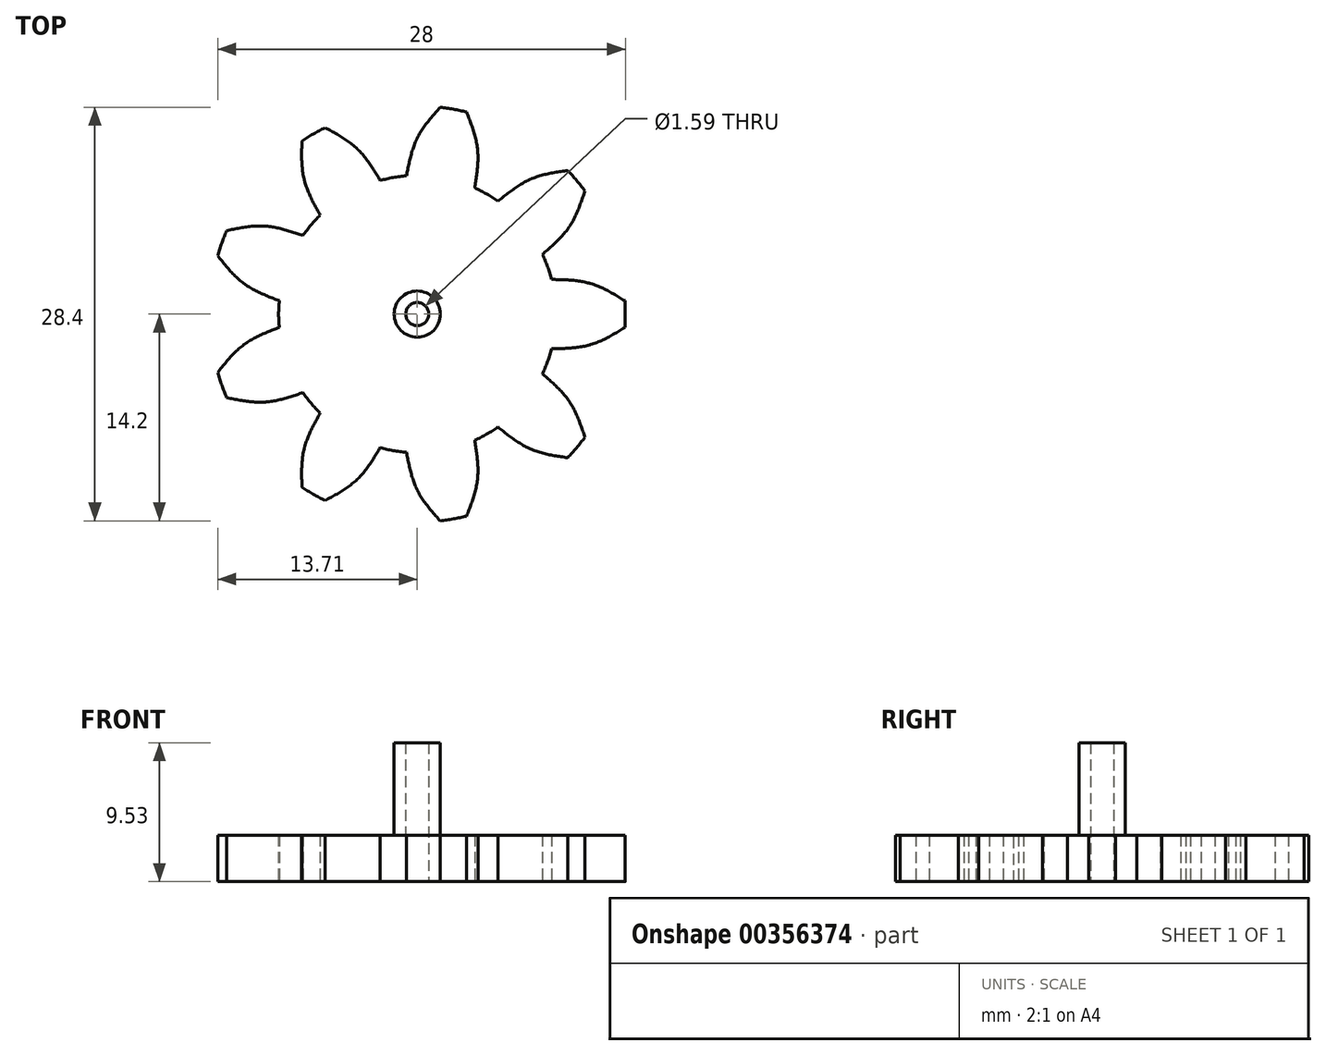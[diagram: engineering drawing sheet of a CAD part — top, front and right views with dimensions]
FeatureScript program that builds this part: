
annotation { "Feature Type Name" : "Feature", "Feature Type Description" : "" }
export const myFeature = defineFeature(function(context is Context, id is Id, definition is map)
    precondition{}
    {
        {
            var Q0;
            Q0=qCreatedBy(makeId("Top.planeOp"),FACE);
            var sketch = newSketch(context, id + "F0", { "sketchPlane" : qUnion([Q0])});
            skCircle(sketch, "E0", {"center": v(0, 0) * mm, "radius": 50.8 * mm});
            skCircle(sketch, "E1", {"center": v(0, 0) * mm, "radius": 63.5 * mm});
            skCircle(sketch, "E2", {"center": v(0, 0) * mm, "radius": 76.2 * mm});
            skLineSegment(sketch, "E3", {"start": v(0, 0) * mm, "end": v(76.2, 0) * mm});
            skCircle(sketch, "E4.cCircle", {"center": v(0, 0) * mm, "radius": 63.5 * mm, "construction": true});
            skLineSegment(sketch, "E4.0", {"start": v(63.5, 11.2) * mm, "end": v(63.5, -11.2) * mm});
            skLineSegment(sketch, "E4.1", {"start": v(63.5, -11.2) * mm, "end": v(55.84, -32.24) * mm});
            skLineSegment(sketch, "E4.2", {"start": v(55.84, -32.24) * mm, "end": v(41.45, -49.4) * mm});
            skLineSegment(sketch, "E4.3", {"start": v(41.45, -49.4) * mm, "end": v(22.05, -60.6) * mm});
            skLineSegment(sketch, "E4.4", {"start": v(22.05, -60.6) * mm, "end": v(0, -64.48) * mm});
            skLineSegment(sketch, "E4.5", {"start": v(0, -64.48) * mm, "end": v(-22.05, -60.6) * mm});
            skLineSegment(sketch, "E4.6", {"start": v(-22.05, -60.6) * mm, "end": v(-41.45, -49.4) * mm});
            skLineSegment(sketch, "E4.7", {"start": v(-41.45, -49.4) * mm, "end": v(-55.84, -32.24) * mm});
            skLineSegment(sketch, "E4.8", {"start": v(-55.84, -32.24) * mm, "end": v(-63.5, -11.2) * mm});
            skLineSegment(sketch, "E4.9", {"start": v(-63.5, -11.2) * mm, "end": v(-63.5, 11.2) * mm});
            skLineSegment(sketch, "E4.10", {"start": v(-63.5, 11.2) * mm, "end": v(-55.84, 32.24) * mm});
            skLineSegment(sketch, "E4.11", {"start": v(-55.84, 32.24) * mm, "end": v(-41.45, 49.4) * mm});
            skLineSegment(sketch, "E4.12", {"start": v(-41.45, 49.4) * mm, "end": v(-22.05, 60.6) * mm});
            skLineSegment(sketch, "E4.13", {"start": v(-22.05, 60.6) * mm, "end": v(0, 64.48) * mm});
            skLineSegment(sketch, "E4.14", {"start": v(0, 64.48) * mm, "end": v(22.05, 60.6) * mm});
            skLineSegment(sketch, "E4.15", {"start": v(22.05, 60.6) * mm, "end": v(41.45, 49.4) * mm});
            skLineSegment(sketch, "E4.16", {"start": v(41.45, 49.4) * mm, "end": v(55.84, 32.24) * mm});
            skLineSegment(sketch, "E4.17", {"start": v(55.84, 32.24) * mm, "end": v(63.5, 11.2) * mm});
            skPoint(sketch, "E4.0.midPoint", {"position": v(63.5, 0) * mm});
            skLineSegment(sketch, "E5.0", {"start": v(49.19, 12.7) * mm, "end": v(49.19, -12.7) * mm});
            skLineSegment(sketch, "E5.1", {"start": v(49.19, -12.7) * mm, "end": v(45.84, -21.89) * mm});
            skLineSegment(sketch, "E5.2", {"start": v(45.84, -21.89) * mm, "end": v(29.52, -41.35) * mm});
            skLineSegment(sketch, "E5.3", {"start": v(29.52, -41.35) * mm, "end": v(21.05, -46.23) * mm});
            skLineSegment(sketch, "E5.4", {"start": v(21.05, -46.23) * mm, "end": v(-3.97, -50.64) * mm});
            skLineSegment(sketch, "E5.5", {"start": v(-3.97, -50.64) * mm, "end": v(-13.6, -48.95) * mm});
            skLineSegment(sketch, "E5.6", {"start": v(-13.6, -48.95) * mm, "end": v(-35.6, -36.25) * mm});
            skLineSegment(sketch, "E5.7", {"start": v(-35.6, -36.25) * mm, "end": v(-41.88, -28.76) * mm});
            skLineSegment(sketch, "E5.8", {"start": v(-41.88, -28.76) * mm, "end": v(-50.56, -4.89) * mm});
            skLineSegment(sketch, "E5.9", {"start": v(-50.56, -4.89) * mm, "end": v(-50.56, 4.89) * mm});
            skLineSegment(sketch, "E5.10", {"start": v(-50.56, 4.89) * mm, "end": v(-41.88, 28.76) * mm});
            skLineSegment(sketch, "E5.11", {"start": v(-41.88, 28.76) * mm, "end": v(-35.6, 36.25) * mm});
            skLineSegment(sketch, "E5.12", {"start": v(-35.6, 36.25) * mm, "end": v(-13.6, 48.95) * mm});
            skLineSegment(sketch, "E5.13", {"start": v(-13.6, 48.95) * mm, "end": v(-3.97, 50.64) * mm});
            skLineSegment(sketch, "E5.14", {"start": v(-3.97, 50.64) * mm, "end": v(21.05, 46.23) * mm});
            skLineSegment(sketch, "E5.15", {"start": v(21.05, 46.23) * mm, "end": v(29.52, 41.35) * mm});
            skLineSegment(sketch, "E5.16", {"start": v(29.52, 41.35) * mm, "end": v(45.84, 21.89) * mm});
            skLineSegment(sketch, "E5.17", {"start": v(45.84, 21.89) * mm, "end": v(49.19, 12.7) * mm});
            skPoint(sketch, "E5.0.midPoint", {"position": v(49.19, 0) * mm});
            skLineSegment(sketch, "E6", {"start": v(0, 0) * mm, "end": v(58.37, 48.98) * mm});
            skLineSegment(sketch, "E7", {"start": v(0, 0) * mm, "end": v(13.23, 75.04) * mm});
            skLineSegment(sketch, "E8", {"start": v(0, 0) * mm, "end": v(-38.1, 66) * mm});
            skLineSegment(sketch, "E9", {"start": v(0, 0) * mm, "end": v(-71.6, 26.06) * mm});
            skLineSegment(sketch, "E10", {"start": v(0, 0) * mm, "end": v(-71.6, -26.06) * mm});
            skLineSegment(sketch, "E11", {"start": v(0, 0) * mm, "end": v(-38.1, -66) * mm});
            skLineSegment(sketch, "E12", {"start": v(-38.1, -66) * mm, "end": v(0, 0) * mm});
            skLineSegment(sketch, "E13", {"start": v(0, 0) * mm, "end": v(13.23, -75.04) * mm});
            skLineSegment(sketch, "E14", {"start": v(13.23, -75.04) * mm, "end": v(0, 0) * mm});
            skLineSegment(sketch, "E15", {"start": v(0, 0) * mm, "end": v(58.37, -48.98) * mm});
            skLineSegment(sketch, "E16", {"start": v(76.04, 4.89) * mm, "end": v(76.04, -4.89) * mm});
            skLineSegment(sketch, "E17", {"start": v(61.4, -45.13) * mm, "end": v(55.1, -52.62) * mm});
            skLineSegment(sketch, "E18", {"start": v(8.4, -75.74) * mm, "end": v(18.02, -74.04) * mm});
            skLineSegment(sketch, "E19", {"start": v(-42.26, -63.41) * mm, "end": v(-33.79, -68.3) * mm});
            skLineSegment(sketch, "E20", {"start": v(-73.13, -21.41) * mm, "end": v(-69.78, -30.6) * mm});
            skLineSegment(sketch, "E21", {"start": v(-73.13, 21.41) * mm, "end": v(-69.78, 30.6) * mm});
            skLineSegment(sketch, "E22", {"start": v(-42.26, 63.41) * mm, "end": v(-33.79, 68.3) * mm});
            skLineSegment(sketch, "E23", {"start": v(8.4, 75.74) * mm, "end": v(18.02, 74.04) * mm});
            skLineSegment(sketch, "E24", {"start": v(55.1, 52.62) * mm, "end": v(61.4, 45.13) * mm});
            skFitSpline(sketch, "E25", {"points": [v(-42.26, 63.41) * mm, v(-41.45, 49.4) * mm, v(-35.6, 36.25) * mm], "startDerivative": vector(-0.86, -28.72) * mm, "endDerivative": vector(14.16, -25.61) * mm});
            skFitSpline(sketch, "E26", {"points": [v(-33.79, 68.3) * mm, v(-22.05, 60.6) * mm, v(-13.6, 48.95) * mm], "startDerivative": vector(25.3, -13.62) * mm, "endDerivative": vector(15.1, -25.06) * mm});
            skFitSpline(sketch, "E27", {"points": [v(8.4, 75.74) * mm, v(0, 64.48) * mm, v(-3.97, 50.64) * mm], "startDerivative": vector(-19.12, -21.45) * mm, "endDerivative": vector(-5.62, -28.72) * mm});
            skFitSpline(sketch, "E28", {"points": [v(18.02, 74.04) * mm, v(22.05, 60.6) * mm, v(21.05, 46.23) * mm], "startDerivative": vector(10.63, -26.7) * mm, "endDerivative": vector(-4.54, -28.9) * mm});
            skFitSpline(sketch, "E29", {"points": [v(29.52, 41.35) * mm, v(41.45, 49.4) * mm, v(55.1, 52.62) * mm], "startDerivative": vector(22.76, 18.39) * mm, "endDerivative": vector(28.44, 4.14) * mm});
            skFitSpline(sketch, "E30", {"points": [v(61.4, 45.13) * mm, v(55.84, 32.24) * mm, v(45.84, 21.89) * mm], "startDerivative": vector(-9.02, -27.29) * mm, "endDerivative": vector(-22.06, -19.22) * mm});
            skFitSpline(sketch, "E31", {"points": [v(49.19, 12.7) * mm, v(63.5, 11.2) * mm, v(76.04, 4.89) * mm], "startDerivative": vector(29.26, -0.55) * mm, "endDerivative": vector(24.45, -15.1) * mm});
            skFitSpline(sketch, "E32", {"points": [v(76.04, -4.89) * mm, v(63.5, -11.2) * mm, v(49.19, -12.7) * mm], "startDerivative": vector(-24.45, -15.1) * mm, "endDerivative": vector(-29.26, -0.55) * mm});
            skFitSpline(sketch, "E33", {"points": [v(45.84, -21.89) * mm, v(55.84, -32.24) * mm, v(61.4, -45.13) * mm], "startDerivative": vector(22.06, -19.22) * mm, "endDerivative": vector(9.02, -27.29) * mm});
            skFitSpline(sketch, "E34", {"points": [v(29.52, -41.35) * mm, v(41.45, -49.4) * mm, v(55.1, -52.62) * mm], "startDerivative": vector(22.76, -18.39) * mm, "endDerivative": vector(28.44, -4.14) * mm});
            skFitSpline(sketch, "E35", {"points": [v(21.05, -46.23) * mm, v(22.05, -60.6) * mm, v(18.02, -74.04) * mm], "startDerivative": vector(4.54, -28.9) * mm, "endDerivative": vector(-10.63, -26.7) * mm});
            skFitSpline(sketch, "E36", {"points": [v(-3.97, -50.64) * mm, v(0, -64.48) * mm, v(8.4, -75.74) * mm], "startDerivative": vector(5.62, -28.72) * mm, "endDerivative": vector(19.12, -21.45) * mm});
            skFitSpline(sketch, "E37", {"points": [v(-13.6, -48.95) * mm, v(-22.05, -60.6) * mm, v(-33.79, -68.3) * mm], "startDerivative": vector(-15.1, -25.06) * mm, "endDerivative": vector(-25.3, -13.62) * mm});
            skFitSpline(sketch, "E38", {"points": [v(-35.6, -36.25) * mm, v(-41.45, -49.4) * mm, v(-42.26, -63.41) * mm], "startDerivative": vector(-14.16, -25.61) * mm, "endDerivative": vector(0.86, -28.72) * mm});
            skFitSpline(sketch, "E39", {"points": [v(-41.88, -28.76) * mm, v(-55.84, -32.24) * mm, v(-69.78, -30.6) * mm], "startDerivative": vector(-27.68, -9.5) * mm, "endDerivative": vector(-28.14, 5.83) * mm});
            skFitSpline(sketch, "E40", {"points": [v(-50.56, -4.89) * mm, v(-63.5, -11.2) * mm, v(-73.13, -21.41) * mm], "startDerivative": vector(-27.3, -10.52) * mm, "endDerivative": vector(-17.8, -22.56) * mm});
            skFitSpline(sketch, "E41", {"points": [v(-41.88, 28.76) * mm, v(-55.84, 32.24) * mm, v(-69.78, 30.6) * mm], "startDerivative": vector(-27.68, 9.5) * mm, "endDerivative": vector(-28.14, -5.83) * mm});
            skFitSpline(sketch, "E42", {"points": [v(-73.13, 21.41) * mm, v(-63.5, 11.2) * mm, v(-50.56, 4.89) * mm], "startDerivative": vector(17.8, -22.56) * mm, "endDerivative": vector(27.3, -10.52) * mm});
            skSolve(sketch);
        }
        {
            var Q0;
            {var subQ0=sQuery(id+"F0.wireOp",EDGE,"E5.2");var subQ3=sQuery(id+"F0.wireOp",EDGE,"E15");var subQ5=makeQuery(id+"F0.imprint","INTERSECT",VERTEX,{"derivedFrom":[subQ0,subQ3]});Q0=makeQuery(id+"F0.imprint","IMPRINT",FACE,{"disambiguationData":[TD([[makeQuery(id+"F0.imprint","IMPRINT",EDGE,{"disambiguationData":[TD([[subQ5,-1.0]])],"derivedFrom":subQ3}),1.0]])]});}
            var Q1;
            {var subQ1=sQuery(id+"F0.wireOp",EDGE,"E5.11");Q1=makeQuery(id+"F0.imprint","IMPRINT",FACE,{"disambiguationData":[TD([[makeQuery(id+"F0.imprint","IMPRINT",EDGE,{"derivedFrom":subQ1}),-1.0]])]});}
            var Q2;
            {var subQ0=sQuery(id+"F0.wireOp",EDGE,"E40");var subQ5=sQuery(id+"F0.wireOp",EDGE,"E1");var subQ7=makeQuery(id+"F0.imprint","INTERSECT",VERTEX,{"derivedFrom":[subQ5,subQ0]});Q2=makeQuery(id+"F0.imprint","IMPRINT",FACE,{"disambiguationData":[TD([[makeQuery(id+"F0.imprint","IMPRINT",EDGE,{"disambiguationData":[TD([[subQ7,-1.0]])],"derivedFrom":subQ5}),1.0]])]});}
            var Q3;
            {var subQ0=sQuery(id+"F0.wireOp",EDGE,"E11");var subQ5=sQuery(id+"F0.wireOp",EDGE,"E19");var subQ7=makeQuery(id+"F0.imprint","INTERSECT",VERTEX,{"derivedFrom":[subQ0,subQ5]});Q3=makeQuery(id+"F0.imprint","IMPRINT",FACE,{"disambiguationData":[TD([[makeQuery(id+"F0.imprint","IMPRINT",EDGE,{"disambiguationData":[TD([[subQ7,1.0]])],"derivedFrom":subQ0}),-1.0]])]});}
            var Q4;
            {var subQ0=sQuery(id+"F0.wireOp",EDGE,"E8");var subQ5=sQuery(id+"F0.wireOp",EDGE,"E22");var subQ7=makeQuery(id+"F0.imprint","INTERSECT",VERTEX,{"derivedFrom":[subQ0,subQ5]});Q4=makeQuery(id+"F0.imprint","IMPRINT",FACE,{"disambiguationData":[TD([[makeQuery(id+"F0.imprint","IMPRINT",EDGE,{"disambiguationData":[TD([[subQ7,1.0]])],"derivedFrom":subQ0}),-1.0]])]});}
            var Q5;
            {var subQ3=sQuery(id+"F0.wireOp",EDGE,"E7");var subQ5=sQuery(id+"F0.wireOp",EDGE,"E23");var subQ6=makeQuery(id+"F0.imprint","INTERSECT",VERTEX,{"derivedFrom":[subQ3,subQ5]});Q5=makeQuery(id+"F0.imprint","IMPRINT",FACE,{"disambiguationData":[TD([[makeQuery(id+"F0.imprint","IMPRINT",EDGE,{"disambiguationData":[TD([[subQ6,1.0]])],"derivedFrom":subQ3}),-1.0]])]});}
            var Q6;
            {var subQ3=sQuery(id+"F0.wireOp",EDGE,"E13");var subQ5=sQuery(id+"F0.wireOp",EDGE,"E18");var subQ6=makeQuery(id+"F0.imprint","INTERSECT",VERTEX,{"derivedFrom":[subQ3,subQ5]});Q6=makeQuery(id+"F0.imprint","IMPRINT",FACE,{"disambiguationData":[TD([[makeQuery(id+"F0.imprint","IMPRINT",EDGE,{"disambiguationData":[TD([[subQ6,1.0]])],"derivedFrom":subQ3}),-1.0]])]});}
            var Q7;
            {var subQ5=sQuery(id+"F0.wireOp",EDGE,"E5.9");Q7=makeQuery(id+"F0.imprint","IMPRINT",FACE,{"disambiguationData":[TD([[makeQuery(id+"F0.imprint","IMPRINT",EDGE,{"derivedFrom":subQ5}),-1.0]])]});}
            var Q8;
            {var subQ0=sQuery(id+"F0.wireOp",EDGE,"E32");var subQ5=sQuery(id+"F0.wireOp",EDGE,"E1");var subQ7=makeQuery(id+"F0.imprint","INTERSECT",VERTEX,{"derivedFrom":[subQ5,subQ0]});Q8=makeQuery(id+"F0.imprint","IMPRINT",FACE,{"disambiguationData":[TD([[makeQuery(id+"F0.imprint","IMPRINT",EDGE,{"disambiguationData":[TD([[subQ7,-1.0]])],"derivedFrom":subQ5}),1.0]])]});}
            var Q9;
            {var subQ3=sQuery(id+"F0.wireOp",EDGE,"E10");var subQ5=sQuery(id+"F0.wireOp",EDGE,"E20");var subQ7=makeQuery(id+"F0.imprint","INTERSECT",VERTEX,{"derivedFrom":[subQ3,subQ5]});Q9=makeQuery(id+"F0.imprint","IMPRINT",FACE,{"disambiguationData":[TD([[makeQuery(id+"F0.imprint","IMPRINT",EDGE,{"disambiguationData":[TD([[subQ7,1.0]])],"derivedFrom":subQ3}),1.0]])]});}
            var Q10;
            {var subQ1=sQuery(id+"F0.wireOp",EDGE,"E0");var subQ3=sQuery(id+"F0.wireOp",EDGE,"E9");var subQ4=makeQuery(id+"F0.imprint","INTERSECT",VERTEX,{"derivedFrom":[subQ1,subQ3]});Q10=makeQuery(id+"F0.imprint","IMPRINT",FACE,{"disambiguationData":[TD([[makeQuery(id+"F0.imprint","IMPRINT",EDGE,{"disambiguationData":[TD([[subQ4,1.0]])],"derivedFrom":subQ3}),-1.0]])]});}
            var Q11;
            {var subQ0=sQuery(id+"F0.wireOp",EDGE,"E5.17");Q11=makeQuery(id+"F0.imprint","IMPRINT",FACE,{"disambiguationData":[TD([[makeQuery(id+"F0.imprint","IMPRINT",EDGE,{"derivedFrom":subQ0}),-1.0]])]});}
            var Q12;
            {var subQ5=sQuery(id+"F0.wireOp",EDGE,"E5.7");Q12=makeQuery(id+"F0.imprint","IMPRINT",FACE,{"disambiguationData":[TD([[makeQuery(id+"F0.imprint","IMPRINT",EDGE,{"derivedFrom":subQ5}),-1.0]])]});}
            var Q13;
            {var subQ0=sQuery(id+"F0.wireOp",EDGE,"E33");var subQ5=sQuery(id+"F0.wireOp",EDGE,"E1");var subQ7=makeQuery(id+"F0.imprint","INTERSECT",VERTEX,{"derivedFrom":[subQ5,subQ0]});Q13=makeQuery(id+"F0.imprint","IMPRINT",FACE,{"disambiguationData":[TD([[makeQuery(id+"F0.imprint","IMPRINT",EDGE,{"disambiguationData":[TD([[subQ7,1.0]])],"derivedFrom":subQ5}),1.0]])]});}
            var Q14;
            {var subQ0=sQuery(id+"F0.wireOp",EDGE,"E27");var subQ5=sQuery(id+"F0.wireOp",EDGE,"E1");var subQ6=makeQuery(id+"F0.imprint","INTERSECT",VERTEX,{"derivedFrom":[subQ5,subQ0]});Q14=makeQuery(id+"F0.imprint","IMPRINT",FACE,{"disambiguationData":[TD([[makeQuery(id+"F0.imprint","IMPRINT",EDGE,{"disambiguationData":[TD([[subQ6,1.0]])],"derivedFrom":subQ5}),1.0]])]});}
            var Q15;
            {var subQ3=sQuery(id+"F0.wireOp",EDGE,"E6");var subQ5=sQuery(id+"F0.wireOp",EDGE,"E24");var subQ6=makeQuery(id+"F0.imprint","INTERSECT",VERTEX,{"derivedFrom":[subQ3,subQ5]});Q15=makeQuery(id+"F0.imprint","IMPRINT",FACE,{"disambiguationData":[TD([[makeQuery(id+"F0.imprint","IMPRINT",EDGE,{"disambiguationData":[TD([[subQ6,1.0]])],"derivedFrom":subQ3}),1.0]])]});}
            var Q16;
            {var subQ1=sQuery(id+"F0.wireOp",EDGE,"E0");var subQ3=sQuery(id+"F0.wireOp",EDGE,"E13");var subQ4=makeQuery(id+"F0.imprint","INTERSECT",VERTEX,{"derivedFrom":[subQ1,subQ3]});Q16=makeQuery(id+"F0.imprint","IMPRINT",FACE,{"disambiguationData":[TD([[makeQuery(id+"F0.imprint","IMPRINT",EDGE,{"disambiguationData":[TD([[subQ4,1.0]])],"derivedFrom":subQ3}),-1.0]])]});}
            var Q17;
            {var subQ0=sQuery(id+"F0.wireOp",EDGE,"E16");var subQ1=sQuery(id+"F0.wireOp",EDGE,"E3");var subQ2=makeQuery(id+"F0.imprint","INTERSECT",VERTEX,{"derivedFrom":[subQ1,subQ0]});Q17=makeQuery(id+"F0.imprint","IMPRINT",FACE,{"disambiguationData":[TD([[makeQuery(id+"F0.imprint","IMPRINT",EDGE,{"disambiguationData":[TD([[subQ2,1.0]])],"derivedFrom":subQ1}),1.0]])]});}
            var Q18;
            {var subQ0=sQuery(id+"F0.wireOp",EDGE,"E15");var subQ5=sQuery(id+"F0.wireOp",EDGE,"E17");var subQ6=makeQuery(id+"F0.imprint","INTERSECT",VERTEX,{"derivedFrom":[subQ0,subQ5]});Q18=makeQuery(id+"F0.imprint","IMPRINT",FACE,{"disambiguationData":[TD([[makeQuery(id+"F0.imprint","IMPRINT",EDGE,{"disambiguationData":[TD([[subQ6,1.0]])],"derivedFrom":subQ0}),1.0]])]});}
            var Q19;
            {var subQ1=sQuery(id+"F0.wireOp",EDGE,"E0");var subQ3=sQuery(id+"F0.wireOp",EDGE,"E13");var subQ4=makeQuery(id+"F0.imprint","INTERSECT",VERTEX,{"derivedFrom":[subQ1,subQ3]});Q19=makeQuery(id+"F0.imprint","IMPRINT",FACE,{"disambiguationData":[TD([[makeQuery(id+"F0.imprint","IMPRINT",EDGE,{"disambiguationData":[TD([[subQ4,1.0]])],"derivedFrom":subQ3}),1.0]])]});}
            var Q20;
            {var subQ1=sQuery(id+"F0.wireOp",EDGE,"E0");var subQ3=sQuery(id+"F0.wireOp",EDGE,"E10");var subQ4=makeQuery(id+"F0.imprint","INTERSECT",VERTEX,{"derivedFrom":[subQ1,subQ3]});Q20=makeQuery(id+"F0.imprint","IMPRINT",FACE,{"disambiguationData":[TD([[makeQuery(id+"F0.imprint","IMPRINT",EDGE,{"disambiguationData":[TD([[subQ4,1.0]])],"derivedFrom":subQ3}),-1.0]])]});}
            var Q21;
            {var subQ1=sQuery(id+"F0.wireOp",EDGE,"E0");var subQ3=sQuery(id+"F0.wireOp",EDGE,"E7");var subQ4=makeQuery(id+"F0.imprint","INTERSECT",VERTEX,{"derivedFrom":[subQ1,subQ3]});Q21=makeQuery(id+"F0.imprint","IMPRINT",FACE,{"disambiguationData":[TD([[makeQuery(id+"F0.imprint","IMPRINT",EDGE,{"disambiguationData":[TD([[subQ4,1.0]])],"derivedFrom":subQ3}),-1.0]])]});}
            var Q22;
            {var subQ0=sQuery(id+"F0.wireOp",EDGE,"E5.1");Q22=makeQuery(id+"F0.imprint","IMPRINT",FACE,{"disambiguationData":[TD([[makeQuery(id+"F0.imprint","IMPRINT",EDGE,{"derivedFrom":subQ0}),-1.0]])]});}
            var Q23;
            {var subQ3=sQuery(id+"F0.wireOp",EDGE,"E9");var subQ5=sQuery(id+"F0.wireOp",EDGE,"E21");var subQ6=makeQuery(id+"F0.imprint","INTERSECT",VERTEX,{"derivedFrom":[subQ3,subQ5]});Q23=makeQuery(id+"F0.imprint","IMPRINT",FACE,{"disambiguationData":[TD([[makeQuery(id+"F0.imprint","IMPRINT",EDGE,{"disambiguationData":[TD([[subQ6,1.0]])],"derivedFrom":subQ3}),1.0]])]});}
            var Q24;
            {var subQ0=sQuery(id+"F0.wireOp",EDGE,"E31");var subQ5=sQuery(id+"F0.wireOp",EDGE,"E1");var subQ6=makeQuery(id+"F0.imprint","INTERSECT",VERTEX,{"derivedFrom":[subQ5,subQ0]});Q24=makeQuery(id+"F0.imprint","IMPRINT",FACE,{"disambiguationData":[TD([[makeQuery(id+"F0.imprint","IMPRINT",EDGE,{"disambiguationData":[TD([[subQ6,1.0]])],"derivedFrom":subQ5}),1.0]])]});}
            var Q25;
            {var subQ0=sQuery(id+"F0.wireOp",EDGE,"E37");var subQ5=sQuery(id+"F0.wireOp",EDGE,"E1");var subQ7=makeQuery(id+"F0.imprint","INTERSECT",VERTEX,{"derivedFrom":[subQ5,subQ0]});Q25=makeQuery(id+"F0.imprint","IMPRINT",FACE,{"disambiguationData":[TD([[makeQuery(id+"F0.imprint","IMPRINT",EDGE,{"disambiguationData":[TD([[subQ7,1.0]])],"derivedFrom":subQ5}),1.0]])]});}
            var Q26;
            {var subQ1=sQuery(id+"F0.wireOp",EDGE,"E0");var subQ3=sQuery(id+"F0.wireOp",EDGE,"E6");var subQ4=makeQuery(id+"F0.imprint","INTERSECT",VERTEX,{"derivedFrom":[subQ1,subQ3]});Q26=makeQuery(id+"F0.imprint","IMPRINT",FACE,{"disambiguationData":[TD([[makeQuery(id+"F0.imprint","IMPRINT",EDGE,{"disambiguationData":[TD([[subQ4,1.0]])],"derivedFrom":subQ3}),-1.0]])]});}
            var Q27;
            {var subQ5=sQuery(id+"F0.wireOp",EDGE,"E5.13");Q27=makeQuery(id+"F0.imprint","IMPRINT",FACE,{"disambiguationData":[TD([[makeQuery(id+"F0.imprint","IMPRINT",EDGE,{"derivedFrom":subQ5}),-1.0]])]});}
            var Q28;
            {var subQ0=sQuery(id+"F0.wireOp",EDGE,"E39");var subQ5=sQuery(id+"F0.wireOp",EDGE,"E1");var subQ7=makeQuery(id+"F0.imprint","INTERSECT",VERTEX,{"derivedFrom":[subQ5,subQ0]});Q28=makeQuery(id+"F0.imprint","IMPRINT",FACE,{"disambiguationData":[TD([[makeQuery(id+"F0.imprint","IMPRINT",EDGE,{"disambiguationData":[TD([[subQ7,1.0]])],"derivedFrom":subQ5}),1.0]])]});}
            var Q29;
            {var subQ0=sQuery(id+"F0.wireOp",EDGE,"E29");var subQ5=sQuery(id+"F0.wireOp",EDGE,"E1");var subQ6=makeQuery(id+"F0.imprint","INTERSECT",VERTEX,{"derivedFrom":[subQ5,subQ0]});Q29=makeQuery(id+"F0.imprint","IMPRINT",FACE,{"disambiguationData":[TD([[makeQuery(id+"F0.imprint","IMPRINT",EDGE,{"disambiguationData":[TD([[subQ6,1.0]])],"derivedFrom":subQ5}),1.0]])]});}
            var Q30;
            {var subQ1=sQuery(id+"F0.wireOp",EDGE,"E0");var subQ3=sQuery(id+"F0.wireOp",EDGE,"E8");var subQ4=makeQuery(id+"F0.imprint","INTERSECT",VERTEX,{"derivedFrom":[subQ1,subQ3]});Q30=makeQuery(id+"F0.imprint","IMPRINT",FACE,{"disambiguationData":[TD([[makeQuery(id+"F0.imprint","IMPRINT",EDGE,{"disambiguationData":[TD([[subQ4,1.0]])],"derivedFrom":subQ3}),-1.0]])]});}
            var Q31;
            {var subQ1=sQuery(id+"F0.wireOp",EDGE,"E0");var subQ3=sQuery(id+"F0.wireOp",EDGE,"E10");var subQ4=makeQuery(id+"F0.imprint","INTERSECT",VERTEX,{"derivedFrom":[subQ1,subQ3]});Q31=makeQuery(id+"F0.imprint","IMPRINT",FACE,{"disambiguationData":[TD([[makeQuery(id+"F0.imprint","IMPRINT",EDGE,{"disambiguationData":[TD([[subQ4,1.0]])],"derivedFrom":subQ3}),1.0]])]});}
            var Q32;
            {var subQ0=sQuery(id+"F0.wireOp",EDGE,"E42");var subQ5=sQuery(id+"F0.wireOp",EDGE,"E1");var subQ6=makeQuery(id+"F0.imprint","INTERSECT",VERTEX,{"derivedFrom":[subQ5,subQ0]});Q32=makeQuery(id+"F0.imprint","IMPRINT",FACE,{"disambiguationData":[TD([[makeQuery(id+"F0.imprint","IMPRINT",EDGE,{"disambiguationData":[TD([[subQ6,1.0]])],"derivedFrom":subQ5}),1.0]])]});}
            var Q33;
            {var subQ0=sQuery(id+"F0.wireOp",EDGE,"E16");var subQ1=sQuery(id+"F0.wireOp",EDGE,"E3");var subQ2=makeQuery(id+"F0.imprint","INTERSECT",VERTEX,{"derivedFrom":[subQ1,subQ0]});Q33=makeQuery(id+"F0.imprint","IMPRINT",FACE,{"disambiguationData":[TD([[makeQuery(id+"F0.imprint","IMPRINT",EDGE,{"disambiguationData":[TD([[subQ2,1.0]])],"derivedFrom":subQ1}),-1.0]])]});}
            var Q34;
            {var subQ1=sQuery(id+"F0.wireOp",EDGE,"E0");var subQ3=sQuery(id+"F0.wireOp",EDGE,"E11");var subQ4=makeQuery(id+"F0.imprint","INTERSECT",VERTEX,{"derivedFrom":[subQ1,subQ3]});Q34=makeQuery(id+"F0.imprint","IMPRINT",FACE,{"disambiguationData":[TD([[makeQuery(id+"F0.imprint","IMPRINT",EDGE,{"disambiguationData":[TD([[subQ4,1.0]])],"derivedFrom":subQ3}),-1.0]])]});}
            var Q35;
            {var subQ0=sQuery(id+"F0.wireOp",EDGE,"E38");var subQ5=sQuery(id+"F0.wireOp",EDGE,"E1");var subQ7=makeQuery(id+"F0.imprint","INTERSECT",VERTEX,{"derivedFrom":[subQ5,subQ0]});Q35=makeQuery(id+"F0.imprint","IMPRINT",FACE,{"disambiguationData":[TD([[makeQuery(id+"F0.imprint","IMPRINT",EDGE,{"disambiguationData":[TD([[subQ7,-1.0]])],"derivedFrom":subQ5}),1.0]])]});}
            var Q36;
            {var subQ1=sQuery(id+"F0.wireOp",EDGE,"E0");var subQ3=sQuery(id+"F0.wireOp",EDGE,"E8");var subQ4=makeQuery(id+"F0.imprint","INTERSECT",VERTEX,{"derivedFrom":[subQ1,subQ3]});Q36=makeQuery(id+"F0.imprint","IMPRINT",FACE,{"disambiguationData":[TD([[makeQuery(id+"F0.imprint","IMPRINT",EDGE,{"disambiguationData":[TD([[subQ4,1.0]])],"derivedFrom":subQ3}),1.0]])]});}
            var Q37;
            {var subQ0=sQuery(id+"F0.wireOp",EDGE,"E26");var subQ5=sQuery(id+"F0.wireOp",EDGE,"E1");var subQ7=makeQuery(id+"F0.imprint","INTERSECT",VERTEX,{"derivedFrom":[subQ5,subQ0]});Q37=makeQuery(id+"F0.imprint","IMPRINT",FACE,{"disambiguationData":[TD([[makeQuery(id+"F0.imprint","IMPRINT",EDGE,{"disambiguationData":[TD([[subQ7,-1.0]])],"derivedFrom":subQ5}),1.0]])]});}
            var Q38;
            {var subQ1=sQuery(id+"F0.wireOp",EDGE,"E0");var subQ3=sQuery(id+"F0.wireOp",EDGE,"E7");var subQ4=makeQuery(id+"F0.imprint","INTERSECT",VERTEX,{"derivedFrom":[subQ1,subQ3]});Q38=makeQuery(id+"F0.imprint","IMPRINT",FACE,{"disambiguationData":[TD([[makeQuery(id+"F0.imprint","IMPRINT",EDGE,{"disambiguationData":[TD([[subQ4,1.0]])],"derivedFrom":subQ3}),1.0]])]});}
            var Q39;
            {var subQ0=sQuery(id+"F0.wireOp",EDGE,"E30");var subQ5=sQuery(id+"F0.wireOp",EDGE,"E1");var subQ7=makeQuery(id+"F0.imprint","INTERSECT",VERTEX,{"derivedFrom":[subQ5,subQ0]});Q39=makeQuery(id+"F0.imprint","IMPRINT",FACE,{"disambiguationData":[TD([[makeQuery(id+"F0.imprint","IMPRINT",EDGE,{"disambiguationData":[TD([[subQ7,-1.0]])],"derivedFrom":subQ5}),1.0]])]});}
            var Q40;
            {var subQ5=sQuery(id+"F0.wireOp",EDGE,"E5.3");Q40=makeQuery(id+"F0.imprint","IMPRINT",FACE,{"disambiguationData":[TD([[makeQuery(id+"F0.imprint","IMPRINT",EDGE,{"derivedFrom":subQ5}),-1.0]])]});}
            var Q41;
            {var subQ1=sQuery(id+"F0.wireOp",EDGE,"E0");var subQ3=sQuery(id+"F0.wireOp",EDGE,"E9");var subQ4=makeQuery(id+"F0.imprint","INTERSECT",VERTEX,{"derivedFrom":[subQ1,subQ3]});Q41=makeQuery(id+"F0.imprint","IMPRINT",FACE,{"disambiguationData":[TD([[makeQuery(id+"F0.imprint","IMPRINT",EDGE,{"disambiguationData":[TD([[subQ4,1.0]])],"derivedFrom":subQ3}),1.0]])]});}
            var Q42;
            {var subQ0=sQuery(id+"F0.wireOp",EDGE,"E28");var subQ5=sQuery(id+"F0.wireOp",EDGE,"E1");var subQ6=makeQuery(id+"F0.imprint","INTERSECT",VERTEX,{"derivedFrom":[subQ5,subQ0]});Q42=makeQuery(id+"F0.imprint","IMPRINT",FACE,{"disambiguationData":[TD([[makeQuery(id+"F0.imprint","IMPRINT",EDGE,{"disambiguationData":[TD([[subQ6,-1.0]])],"derivedFrom":subQ5}),1.0]])]});}
            var Q43;
            {var subQ3=sQuery(id+"F0.wireOp",EDGE,"E7");var subQ5=sQuery(id+"F0.wireOp",EDGE,"E23");var subQ6=makeQuery(id+"F0.imprint","INTERSECT",VERTEX,{"derivedFrom":[subQ3,subQ5]});Q43=makeQuery(id+"F0.imprint","IMPRINT",FACE,{"disambiguationData":[TD([[makeQuery(id+"F0.imprint","IMPRINT",EDGE,{"disambiguationData":[TD([[subQ6,1.0]])],"derivedFrom":subQ3}),1.0]])]});}
            var Q44;
            {var subQ0=sQuery(id+"F0.wireOp",EDGE,"E34");var subQ5=sQuery(id+"F0.wireOp",EDGE,"E1");var subQ7=makeQuery(id+"F0.imprint","INTERSECT",VERTEX,{"derivedFrom":[subQ5,subQ0]});Q44=makeQuery(id+"F0.imprint","IMPRINT",FACE,{"disambiguationData":[TD([[makeQuery(id+"F0.imprint","IMPRINT",EDGE,{"disambiguationData":[TD([[subQ7,-1.0]])],"derivedFrom":subQ5}),1.0]])]});}
            var Q45;
            {var subQ3=sQuery(id+"F0.wireOp",EDGE,"E9");var subQ5=sQuery(id+"F0.wireOp",EDGE,"E21");var subQ7=makeQuery(id+"F0.imprint","INTERSECT",VERTEX,{"derivedFrom":[subQ3,subQ5]});Q45=makeQuery(id+"F0.imprint","IMPRINT",FACE,{"disambiguationData":[TD([[makeQuery(id+"F0.imprint","IMPRINT",EDGE,{"disambiguationData":[TD([[subQ7,1.0]])],"derivedFrom":subQ3}),-1.0]])]});}
            var Q46;
            {var subQ0=sQuery(id+"F0.wireOp",EDGE,"E25");var subQ5=sQuery(id+"F0.wireOp",EDGE,"E1");var subQ7=makeQuery(id+"F0.imprint","INTERSECT",VERTEX,{"derivedFrom":[subQ5,subQ0]});Q46=makeQuery(id+"F0.imprint","IMPRINT",FACE,{"disambiguationData":[TD([[makeQuery(id+"F0.imprint","IMPRINT",EDGE,{"disambiguationData":[TD([[subQ7,1.0]])],"derivedFrom":subQ5}),1.0]])]});}
            var Q47;
            {var subQ0=sQuery(id+"F0.wireOp",EDGE,"E6");var subQ5=sQuery(id+"F0.wireOp",EDGE,"E24");var subQ6=makeQuery(id+"F0.imprint","INTERSECT",VERTEX,{"derivedFrom":[subQ0,subQ5]});Q47=makeQuery(id+"F0.imprint","IMPRINT",FACE,{"disambiguationData":[TD([[makeQuery(id+"F0.imprint","IMPRINT",EDGE,{"disambiguationData":[TD([[subQ6,1.0]])],"derivedFrom":subQ0}),-1.0]])]});}
            var Q48;
            {var subQ1=sQuery(id+"F0.wireOp",EDGE,"E5.15");Q48=makeQuery(id+"F0.imprint","IMPRINT",FACE,{"disambiguationData":[TD([[makeQuery(id+"F0.imprint","IMPRINT",EDGE,{"derivedFrom":subQ1}),-1.0]])]});}
            var Q49;
            {var subQ0=sQuery(id+"F0.wireOp",EDGE,"E36");var subQ5=sQuery(id+"F0.wireOp",EDGE,"E1");var subQ6=makeQuery(id+"F0.imprint","INTERSECT",VERTEX,{"derivedFrom":[subQ5,subQ0]});Q49=makeQuery(id+"F0.imprint","IMPRINT",FACE,{"disambiguationData":[TD([[makeQuery(id+"F0.imprint","IMPRINT",EDGE,{"disambiguationData":[TD([[subQ6,-1.0]])],"derivedFrom":subQ5}),1.0]])]});}
            var Q50;
            {var subQ0=sQuery(id+"F0.wireOp",EDGE,"E41");var subQ5=sQuery(id+"F0.wireOp",EDGE,"E1");var subQ6=makeQuery(id+"F0.imprint","INTERSECT",VERTEX,{"derivedFrom":[subQ5,subQ0]});Q50=makeQuery(id+"F0.imprint","IMPRINT",FACE,{"disambiguationData":[TD([[makeQuery(id+"F0.imprint","IMPRINT",EDGE,{"disambiguationData":[TD([[subQ6,-1.0]])],"derivedFrom":subQ5}),1.0]])]});}
            var Q51;
            {var subQ0=sQuery(id+"F0.wireOp",EDGE,"E10");var subQ5=sQuery(id+"F0.wireOp",EDGE,"E20");var subQ7=makeQuery(id+"F0.imprint","INTERSECT",VERTEX,{"derivedFrom":[subQ0,subQ5]});Q51=makeQuery(id+"F0.imprint","IMPRINT",FACE,{"disambiguationData":[TD([[makeQuery(id+"F0.imprint","IMPRINT",EDGE,{"disambiguationData":[TD([[subQ7,1.0]])],"derivedFrom":subQ0}),-1.0]])]});}
            var Q52;
            {var subQ3=sQuery(id+"F0.wireOp",EDGE,"E11");var subQ5=sQuery(id+"F0.wireOp",EDGE,"E19");var subQ6=makeQuery(id+"F0.imprint","INTERSECT",VERTEX,{"derivedFrom":[subQ3,subQ5]});Q52=makeQuery(id+"F0.imprint","IMPRINT",FACE,{"disambiguationData":[TD([[makeQuery(id+"F0.imprint","IMPRINT",EDGE,{"disambiguationData":[TD([[subQ6,1.0]])],"derivedFrom":subQ3}),1.0]])]});}
            var Q53;
            {var subQ0=sQuery(id+"F0.wireOp",EDGE,"E15");var subQ5=sQuery(id+"F0.wireOp",EDGE,"E17");var subQ6=makeQuery(id+"F0.imprint","INTERSECT",VERTEX,{"derivedFrom":[subQ0,subQ5]});Q53=makeQuery(id+"F0.imprint","IMPRINT",FACE,{"disambiguationData":[TD([[makeQuery(id+"F0.imprint","IMPRINT",EDGE,{"disambiguationData":[TD([[subQ6,1.0]])],"derivedFrom":subQ0}),-1.0]])]});}
            var Q54;
            {var subQ0=sQuery(id+"F0.wireOp",EDGE,"E35");var subQ5=sQuery(id+"F0.wireOp",EDGE,"E1");var subQ6=makeQuery(id+"F0.imprint","INTERSECT",VERTEX,{"derivedFrom":[subQ5,subQ0]});Q54=makeQuery(id+"F0.imprint","IMPRINT",FACE,{"disambiguationData":[TD([[makeQuery(id+"F0.imprint","IMPRINT",EDGE,{"disambiguationData":[TD([[subQ6,1.0]])],"derivedFrom":subQ5}),1.0]])]});}
            var Q55;
            {var subQ0=sQuery(id+"F0.wireOp",EDGE,"E8");var subQ5=sQuery(id+"F0.wireOp",EDGE,"E22");var subQ6=makeQuery(id+"F0.imprint","INTERSECT",VERTEX,{"derivedFrom":[subQ0,subQ5]});Q55=makeQuery(id+"F0.imprint","IMPRINT",FACE,{"disambiguationData":[TD([[makeQuery(id+"F0.imprint","IMPRINT",EDGE,{"disambiguationData":[TD([[subQ6,1.0]])],"derivedFrom":subQ0}),1.0]])]});}
            var Q56;
            {var subQ3=sQuery(id+"F0.wireOp",EDGE,"E13");var subQ5=sQuery(id+"F0.wireOp",EDGE,"E18");var subQ7=makeQuery(id+"F0.imprint","INTERSECT",VERTEX,{"derivedFrom":[subQ3,subQ5]});Q56=makeQuery(id+"F0.imprint","IMPRINT",FACE,{"disambiguationData":[TD([[makeQuery(id+"F0.imprint","IMPRINT",EDGE,{"disambiguationData":[TD([[subQ7,1.0]])],"derivedFrom":subQ3}),1.0]])]});}
            var Q57;
            {var subQ1=sQuery(id+"F0.wireOp",EDGE,"E5.5");Q57=makeQuery(id+"F0.imprint","IMPRINT",FACE,{"disambiguationData":[TD([[makeQuery(id+"F0.imprint","IMPRINT",EDGE,{"derivedFrom":subQ1}),-1.0]])]});}
            var Q58;
            {var subQ0=sQuery(id+"F0.wireOp",EDGE,"E5.7");Q58=makeQuery(id+"F0.imprint","IMPRINT",FACE,{"disambiguationData":[TD([[makeQuery(id+"F0.imprint","IMPRINT",EDGE,{"derivedFrom":subQ0}),1.0]])]});}
            var Q59;
            {var subQ0=sQuery(id+"F0.wireOp",EDGE,"E3");var subQ1=sQuery(id+"F0.wireOp",EDGE,"E2");var subQ2=makeQuery(id+"F0.imprint","INTERSECT",VERTEX,{"derivedFrom":[subQ1,subQ0]});Q59=makeQuery(id+"F0.imprint","IMPRINT",FACE,{"disambiguationData":[TD([[makeQuery(id+"F0.imprint","IMPRINT",EDGE,{"disambiguationData":[TD([[subQ2,1.0]])],"derivedFrom":subQ0}),-1.0]])]});}
            var Q60;
            {var subQ1=sQuery(id+"F0.wireOp",EDGE,"E0");var subQ3=sQuery(id+"F0.wireOp",EDGE,"E3");var subQ4=makeQuery(id+"F0.imprint","INTERSECT",VERTEX,{"derivedFrom":[subQ1,subQ3]});Q60=makeQuery(id+"F0.imprint","IMPRINT",FACE,{"disambiguationData":[TD([[makeQuery(id+"F0.imprint","IMPRINT",EDGE,{"disambiguationData":[TD([[subQ4,1.0]])],"derivedFrom":subQ3}),-1.0]])]});}
            var Q61;
            {var subQ0=sQuery(id+"F0.wireOp",EDGE,"E5.13");Q61=makeQuery(id+"F0.imprint","IMPRINT",FACE,{"disambiguationData":[TD([[makeQuery(id+"F0.imprint","IMPRINT",EDGE,{"derivedFrom":subQ0}),1.0]])]});}
            var Q62;
            {var subQ1=sQuery(id+"F0.wireOp",EDGE,"E1");var subQ3=sQuery(id+"F0.wireOp",EDGE,"E29");var subQ4=makeQuery(id+"F0.imprint","INTERSECT",VERTEX,{"derivedFrom":[subQ1,subQ3]});Q62=makeQuery(id+"F0.imprint","IMPRINT",FACE,{"disambiguationData":[TD([[makeQuery(id+"F0.imprint","IMPRINT",EDGE,{"disambiguationData":[TD([[subQ4,1.0]])],"derivedFrom":subQ1}),-1.0]])]});}
            var Q63;
            {var subQ1=sQuery(id+"F0.wireOp",EDGE,"E1");var subQ3=sQuery(id+"F0.wireOp",EDGE,"E25");var subQ4=makeQuery(id+"F0.imprint","INTERSECT",VERTEX,{"derivedFrom":[subQ1,subQ3]});Q63=makeQuery(id+"F0.imprint","IMPRINT",FACE,{"disambiguationData":[TD([[makeQuery(id+"F0.imprint","IMPRINT",EDGE,{"disambiguationData":[TD([[subQ4,1.0]])],"derivedFrom":subQ1}),-1.0]])]});}
            var Q64;
            {var subQ1=sQuery(id+"F0.wireOp",EDGE,"E1");var subQ3=sQuery(id+"F0.wireOp",EDGE,"E39");var subQ4=makeQuery(id+"F0.imprint","INTERSECT",VERTEX,{"derivedFrom":[subQ1,subQ3]});Q64=makeQuery(id+"F0.imprint","IMPRINT",FACE,{"disambiguationData":[TD([[makeQuery(id+"F0.imprint","IMPRINT",EDGE,{"disambiguationData":[TD([[subQ4,1.0]])],"derivedFrom":subQ1}),-1.0]])]});}
            var Q65;
            {var subQ0=sQuery(id+"F0.wireOp",EDGE,"E5.9");Q65=makeQuery(id+"F0.imprint","IMPRINT",FACE,{"disambiguationData":[TD([[makeQuery(id+"F0.imprint","IMPRINT",EDGE,{"derivedFrom":subQ0}),1.0]])]});}
            var Q66;
            {var subQ0=sQuery(id+"F0.wireOp",EDGE,"E5.3");Q66=makeQuery(id+"F0.imprint","IMPRINT",FACE,{"disambiguationData":[TD([[makeQuery(id+"F0.imprint","IMPRINT",EDGE,{"derivedFrom":subQ0}),1.0]])]});}
            var Q67;
            {var subQ1=sQuery(id+"F0.wireOp",EDGE,"E0");var subQ3=sQuery(id+"F0.wireOp",EDGE,"E11");var subQ4=makeQuery(id+"F0.imprint","INTERSECT",VERTEX,{"derivedFrom":[subQ1,subQ3]});Q67=makeQuery(id+"F0.imprint","IMPRINT",FACE,{"disambiguationData":[TD([[makeQuery(id+"F0.imprint","IMPRINT",EDGE,{"disambiguationData":[TD([[subQ4,1.0]])],"derivedFrom":subQ3}),1.0]])]});}
            var Q68;
            {var subQ1=sQuery(id+"F0.wireOp",EDGE,"E0");var subQ3=sQuery(id+"F0.wireOp",EDGE,"E6");var subQ4=makeQuery(id+"F0.imprint","INTERSECT",VERTEX,{"derivedFrom":[subQ1,subQ3]});Q68=makeQuery(id+"F0.imprint","IMPRINT",FACE,{"disambiguationData":[TD([[makeQuery(id+"F0.imprint","IMPRINT",EDGE,{"disambiguationData":[TD([[subQ4,1.0]])],"derivedFrom":subQ3}),1.0]])]});}
            var Q69;
            {var subQ0=sQuery(id+"F0.wireOp",EDGE,"E5.2");var subQ3=sQuery(id+"F0.wireOp",EDGE,"E15");var subQ5=makeQuery(id+"F0.imprint","INTERSECT",VERTEX,{"derivedFrom":[subQ0,subQ3]});Q69=makeQuery(id+"F0.imprint","IMPRINT",FACE,{"disambiguationData":[TD([[makeQuery(id+"F0.imprint","IMPRINT",EDGE,{"disambiguationData":[TD([[subQ5,-1.0]])],"derivedFrom":subQ3}),-1.0]])]});}
            var Q70;
            {var subQ0=sQuery(id+"F0.wireOp",EDGE,"E8");var subQ1=sQuery(id+"F0.wireOp",EDGE,"E2");var subQ2=makeQuery(id+"F0.imprint","INTERSECT",VERTEX,{"derivedFrom":[subQ1,subQ0]});Q70=makeQuery(id+"F0.imprint","IMPRINT",FACE,{"disambiguationData":[TD([[makeQuery(id+"F0.imprint","IMPRINT",EDGE,{"disambiguationData":[TD([[subQ2,1.0]])],"derivedFrom":subQ0}),-1.0]])]});}
            var Q71;
            {var subQ0=sQuery(id+"F0.wireOp",EDGE,"E5.1");Q71=makeQuery(id+"F0.imprint","IMPRINT",FACE,{"disambiguationData":[TD([[makeQuery(id+"F0.imprint","IMPRINT",EDGE,{"derivedFrom":subQ0}),1.0]])]});}
            var Q72;
            {var subQ0=sQuery(id+"F0.wireOp",EDGE,"E35");var subQ1=sQuery(id+"F0.wireOp",EDGE,"E1");var subQ2=makeQuery(id+"F0.imprint","INTERSECT",VERTEX,{"derivedFrom":[subQ1,subQ0]});Q72=makeQuery(id+"F0.imprint","IMPRINT",FACE,{"disambiguationData":[TD([[makeQuery(id+"F0.imprint","IMPRINT",EDGE,{"disambiguationData":[TD([[subQ2,1.0]])],"derivedFrom":subQ1}),-1.0]])]});}
            var Q73;
            {var subQ1=sQuery(id+"F0.wireOp",EDGE,"E1");var subQ3=sQuery(id+"F0.wireOp",EDGE,"E38");var subQ4=makeQuery(id+"F0.imprint","INTERSECT",VERTEX,{"derivedFrom":[subQ1,subQ3]});Q73=makeQuery(id+"F0.imprint","IMPRINT",FACE,{"disambiguationData":[TD([[makeQuery(id+"F0.imprint","IMPRINT",EDGE,{"disambiguationData":[TD([[subQ4,-1.0]])],"derivedFrom":subQ1}),-1.0]])]});}
            var Q74;
            {var subQ1=sQuery(id+"F0.wireOp",EDGE,"E1");var subQ3=sQuery(id+"F0.wireOp",EDGE,"E34");var subQ4=makeQuery(id+"F0.imprint","INTERSECT",VERTEX,{"derivedFrom":[subQ1,subQ3]});Q74=makeQuery(id+"F0.imprint","IMPRINT",FACE,{"disambiguationData":[TD([[makeQuery(id+"F0.imprint","IMPRINT",EDGE,{"disambiguationData":[TD([[subQ4,-1.0]])],"derivedFrom":subQ1}),-1.0]])]});}
            var Q75;
            {var subQ0=sQuery(id+"F0.wireOp",EDGE,"E3");var subQ1=sQuery(id+"F0.wireOp",EDGE,"E2");var subQ2=makeQuery(id+"F0.imprint","INTERSECT",VERTEX,{"derivedFrom":[subQ1,subQ0]});Q75=makeQuery(id+"F0.imprint","IMPRINT",FACE,{"disambiguationData":[TD([[makeQuery(id+"F0.imprint","IMPRINT",EDGE,{"disambiguationData":[TD([[subQ2,1.0]])],"derivedFrom":subQ0}),1.0]])]});}
            var Q76;
            {var subQ0=sQuery(id+"F0.wireOp",EDGE,"E5.11");Q76=makeQuery(id+"F0.imprint","IMPRINT",FACE,{"disambiguationData":[TD([[makeQuery(id+"F0.imprint","IMPRINT",EDGE,{"derivedFrom":subQ0}),1.0]])]});}
            var Q77;
            {var subQ0=sQuery(id+"F0.wireOp",EDGE,"E5.17");Q77=makeQuery(id+"F0.imprint","IMPRINT",FACE,{"disambiguationData":[TD([[makeQuery(id+"F0.imprint","IMPRINT",EDGE,{"derivedFrom":subQ0}),1.0]])]});}
            var Q78;
            {var subQ0=sQuery(id+"F0.wireOp",EDGE,"E36");var subQ1=sQuery(id+"F0.wireOp",EDGE,"E1");var subQ2=makeQuery(id+"F0.imprint","INTERSECT",VERTEX,{"derivedFrom":[subQ1,subQ0]});Q78=makeQuery(id+"F0.imprint","IMPRINT",FACE,{"disambiguationData":[TD([[makeQuery(id+"F0.imprint","IMPRINT",EDGE,{"disambiguationData":[TD([[subQ2,-1.0]])],"derivedFrom":subQ1}),-1.0]])]});}
            var Q79;
            {var subQ0=sQuery(id+"F0.wireOp",EDGE,"E41");var subQ1=sQuery(id+"F0.wireOp",EDGE,"E1");var subQ2=makeQuery(id+"F0.imprint","INTERSECT",VERTEX,{"derivedFrom":[subQ1,subQ0]});Q79=makeQuery(id+"F0.imprint","IMPRINT",FACE,{"disambiguationData":[TD([[makeQuery(id+"F0.imprint","IMPRINT",EDGE,{"disambiguationData":[TD([[subQ2,-1.0]])],"derivedFrom":subQ1}),-1.0]])]});}
            var Q80;
            {var subQ0=sQuery(id+"F0.wireOp",EDGE,"E5.5");Q80=makeQuery(id+"F0.imprint","IMPRINT",FACE,{"disambiguationData":[TD([[makeQuery(id+"F0.imprint","IMPRINT",EDGE,{"derivedFrom":subQ0}),1.0]])]});}
            var Q81;
            {var subQ0=sQuery(id+"F0.wireOp",EDGE,"E27");var subQ1=sQuery(id+"F0.wireOp",EDGE,"E1");var subQ2=makeQuery(id+"F0.imprint","INTERSECT",VERTEX,{"derivedFrom":[subQ1,subQ0]});Q81=makeQuery(id+"F0.imprint","IMPRINT",FACE,{"disambiguationData":[TD([[makeQuery(id+"F0.imprint","IMPRINT",EDGE,{"disambiguationData":[TD([[subQ2,1.0]])],"derivedFrom":subQ1}),-1.0]])]});}
            var Q82;
            {var subQ1=sQuery(id+"F0.wireOp",EDGE,"E0");var subQ3=sQuery(id+"F0.wireOp",EDGE,"E3");var subQ4=makeQuery(id+"F0.imprint","INTERSECT",VERTEX,{"derivedFrom":[subQ1,subQ3]});Q82=makeQuery(id+"F0.imprint","IMPRINT",FACE,{"disambiguationData":[TD([[makeQuery(id+"F0.imprint","IMPRINT",EDGE,{"disambiguationData":[TD([[subQ4,1.0]])],"derivedFrom":subQ3}),1.0]])]});}
            var Q83;
            {var subQ0=sQuery(id+"F0.wireOp",EDGE,"E28");var subQ1=sQuery(id+"F0.wireOp",EDGE,"E1");var subQ2=makeQuery(id+"F0.imprint","INTERSECT",VERTEX,{"derivedFrom":[subQ1,subQ0]});Q83=makeQuery(id+"F0.imprint","IMPRINT",FACE,{"disambiguationData":[TD([[makeQuery(id+"F0.imprint","IMPRINT",EDGE,{"disambiguationData":[TD([[subQ2,-1.0]])],"derivedFrom":subQ1}),-1.0]])]});}
            var Q84;
            {var subQ0=sQuery(id+"F0.wireOp",EDGE,"E10");var subQ1=sQuery(id+"F0.wireOp",EDGE,"E2");var subQ2=makeQuery(id+"F0.imprint","INTERSECT",VERTEX,{"derivedFrom":[subQ1,subQ0]});Q84=makeQuery(id+"F0.imprint","IMPRINT",FACE,{"disambiguationData":[TD([[makeQuery(id+"F0.imprint","IMPRINT",EDGE,{"disambiguationData":[TD([[subQ2,1.0]])],"derivedFrom":subQ0}),-1.0]])]});}
            var Q85;
            {var subQ1=sQuery(id+"F0.wireOp",EDGE,"E1");var subQ3=sQuery(id+"F0.wireOp",EDGE,"E37");var subQ4=makeQuery(id+"F0.imprint","INTERSECT",VERTEX,{"derivedFrom":[subQ1,subQ3]});Q85=makeQuery(id+"F0.imprint","IMPRINT",FACE,{"disambiguationData":[TD([[makeQuery(id+"F0.imprint","IMPRINT",EDGE,{"disambiguationData":[TD([[subQ4,1.0]])],"derivedFrom":subQ1}),-1.0]])]});}
            var Q86;
            {var subQ0=sQuery(id+"F0.wireOp",EDGE,"E15");var subQ1=sQuery(id+"F0.wireOp",EDGE,"E2");var subQ2=makeQuery(id+"F0.imprint","INTERSECT",VERTEX,{"derivedFrom":[subQ1,subQ0]});Q86=makeQuery(id+"F0.imprint","IMPRINT",FACE,{"disambiguationData":[TD([[makeQuery(id+"F0.imprint","IMPRINT",EDGE,{"disambiguationData":[TD([[subQ2,1.0]])],"derivedFrom":subQ0}),1.0]])]});}
            var Q87;
            {var subQ0=sQuery(id+"F0.wireOp",EDGE,"E7");var subQ1=sQuery(id+"F0.wireOp",EDGE,"E2");var subQ2=makeQuery(id+"F0.imprint","INTERSECT",VERTEX,{"derivedFrom":[subQ1,subQ0]});Q87=makeQuery(id+"F0.imprint","IMPRINT",FACE,{"disambiguationData":[TD([[makeQuery(id+"F0.imprint","IMPRINT",EDGE,{"disambiguationData":[TD([[subQ2,1.0]])],"derivedFrom":subQ0}),-1.0]])]});}
            var Q88;
            {var subQ0=sQuery(id+"F0.wireOp",EDGE,"E6");var subQ1=sQuery(id+"F0.wireOp",EDGE,"E2");var subQ2=makeQuery(id+"F0.imprint","INTERSECT",VERTEX,{"derivedFrom":[subQ1,subQ0]});Q88=makeQuery(id+"F0.imprint","IMPRINT",FACE,{"disambiguationData":[TD([[makeQuery(id+"F0.imprint","IMPRINT",EDGE,{"disambiguationData":[TD([[subQ2,1.0]])],"derivedFrom":subQ0}),1.0]])]});}
            var Q89;
            {var subQ1=sQuery(id+"F0.wireOp",EDGE,"E1");var subQ3=sQuery(id+"F0.wireOp",EDGE,"E26");var subQ4=makeQuery(id+"F0.imprint","INTERSECT",VERTEX,{"derivedFrom":[subQ1,subQ3]});Q89=makeQuery(id+"F0.imprint","IMPRINT",FACE,{"disambiguationData":[TD([[makeQuery(id+"F0.imprint","IMPRINT",EDGE,{"disambiguationData":[TD([[subQ4,-1.0]])],"derivedFrom":subQ1}),-1.0]])]});}
            var Q90;
            {var subQ0=sQuery(id+"F0.wireOp",EDGE,"E5.15");Q90=makeQuery(id+"F0.imprint","IMPRINT",FACE,{"disambiguationData":[TD([[makeQuery(id+"F0.imprint","IMPRINT",EDGE,{"derivedFrom":subQ0}),1.0]])]});}
            var Q91;
            {var subQ0=sQuery(id+"F0.wireOp",EDGE,"E11");var subQ1=sQuery(id+"F0.wireOp",EDGE,"E2");var subQ2=makeQuery(id+"F0.imprint","INTERSECT",VERTEX,{"derivedFrom":[subQ1,subQ0]});Q91=makeQuery(id+"F0.imprint","IMPRINT",FACE,{"disambiguationData":[TD([[makeQuery(id+"F0.imprint","IMPRINT",EDGE,{"disambiguationData":[TD([[subQ2,1.0]])],"derivedFrom":subQ0}),-1.0]])]});}
            var Q92;
            {var subQ1=sQuery(id+"F0.wireOp",EDGE,"E1");var subQ3=sQuery(id+"F0.wireOp",EDGE,"E40");var subQ4=makeQuery(id+"F0.imprint","INTERSECT",VERTEX,{"derivedFrom":[subQ1,subQ3]});Q92=makeQuery(id+"F0.imprint","IMPRINT",FACE,{"disambiguationData":[TD([[makeQuery(id+"F0.imprint","IMPRINT",EDGE,{"disambiguationData":[TD([[subQ4,-1.0]])],"derivedFrom":subQ1}),-1.0]])]});}
            var Q93;
            {var subQ0=sQuery(id+"F0.wireOp",EDGE,"E7");var subQ1=sQuery(id+"F0.wireOp",EDGE,"E2");var subQ2=makeQuery(id+"F0.imprint","INTERSECT",VERTEX,{"derivedFrom":[subQ1,subQ0]});Q93=makeQuery(id+"F0.imprint","IMPRINT",FACE,{"disambiguationData":[TD([[makeQuery(id+"F0.imprint","IMPRINT",EDGE,{"disambiguationData":[TD([[subQ2,1.0]])],"derivedFrom":subQ0}),1.0]])]});}
            var Q94;
            {var subQ0=sQuery(id+"F0.wireOp",EDGE,"E42");var subQ1=sQuery(id+"F0.wireOp",EDGE,"E1");var subQ2=makeQuery(id+"F0.imprint","INTERSECT",VERTEX,{"derivedFrom":[subQ1,subQ0]});Q94=makeQuery(id+"F0.imprint","IMPRINT",FACE,{"disambiguationData":[TD([[makeQuery(id+"F0.imprint","IMPRINT",EDGE,{"disambiguationData":[TD([[subQ2,1.0]])],"derivedFrom":subQ1}),-1.0]])]});}
            var Q95;
            {var subQ0=sQuery(id+"F0.wireOp",EDGE,"E9");var subQ1=sQuery(id+"F0.wireOp",EDGE,"E2");var subQ2=makeQuery(id+"F0.imprint","INTERSECT",VERTEX,{"derivedFrom":[subQ1,subQ0]});Q95=makeQuery(id+"F0.imprint","IMPRINT",FACE,{"disambiguationData":[TD([[makeQuery(id+"F0.imprint","IMPRINT",EDGE,{"disambiguationData":[TD([[subQ2,1.0]])],"derivedFrom":subQ0}),-1.0]])]});}
            var Q96;
            {var subQ0=sQuery(id+"F0.wireOp",EDGE,"E10");var subQ1=sQuery(id+"F0.wireOp",EDGE,"E2");var subQ2=makeQuery(id+"F0.imprint","INTERSECT",VERTEX,{"derivedFrom":[subQ1,subQ0]});Q96=makeQuery(id+"F0.imprint","IMPRINT",FACE,{"disambiguationData":[TD([[makeQuery(id+"F0.imprint","IMPRINT",EDGE,{"disambiguationData":[TD([[subQ2,1.0]])],"derivedFrom":subQ0}),1.0]])]});}
            var Q97;
            {var subQ0=sQuery(id+"F0.wireOp",EDGE,"E15");var subQ1=sQuery(id+"F0.wireOp",EDGE,"E2");var subQ2=makeQuery(id+"F0.imprint","INTERSECT",VERTEX,{"derivedFrom":[subQ1,subQ0]});Q97=makeQuery(id+"F0.imprint","IMPRINT",FACE,{"disambiguationData":[TD([[makeQuery(id+"F0.imprint","IMPRINT",EDGE,{"disambiguationData":[TD([[subQ2,1.0]])],"derivedFrom":subQ0}),-1.0]])]});}
            var Q98;
            {var subQ0=sQuery(id+"F0.wireOp",EDGE,"E6");var subQ1=sQuery(id+"F0.wireOp",EDGE,"E2");var subQ2=makeQuery(id+"F0.imprint","INTERSECT",VERTEX,{"derivedFrom":[subQ1,subQ0]});Q98=makeQuery(id+"F0.imprint","IMPRINT",FACE,{"disambiguationData":[TD([[makeQuery(id+"F0.imprint","IMPRINT",EDGE,{"disambiguationData":[TD([[subQ2,1.0]])],"derivedFrom":subQ0}),-1.0]])]});}
            var Q99;
            {var subQ0=sQuery(id+"F0.wireOp",EDGE,"E9");var subQ1=sQuery(id+"F0.wireOp",EDGE,"E2");var subQ2=makeQuery(id+"F0.imprint","INTERSECT",VERTEX,{"derivedFrom":[subQ1,subQ0]});Q99=makeQuery(id+"F0.imprint","IMPRINT",FACE,{"disambiguationData":[TD([[makeQuery(id+"F0.imprint","IMPRINT",EDGE,{"disambiguationData":[TD([[subQ2,1.0]])],"derivedFrom":subQ0}),1.0]])]});}
            var Q100;
            {var subQ0=sQuery(id+"F0.wireOp",EDGE,"E8");var subQ1=sQuery(id+"F0.wireOp",EDGE,"E2");var subQ2=makeQuery(id+"F0.imprint","INTERSECT",VERTEX,{"derivedFrom":[subQ1,subQ0]});Q100=makeQuery(id+"F0.imprint","IMPRINT",FACE,{"disambiguationData":[TD([[makeQuery(id+"F0.imprint","IMPRINT",EDGE,{"disambiguationData":[TD([[subQ2,1.0]])],"derivedFrom":subQ0}),1.0]])]});}
            var Q101;
            {var subQ1=sQuery(id+"F0.wireOp",EDGE,"E1");var subQ3=sQuery(id+"F0.wireOp",EDGE,"E33");var subQ4=makeQuery(id+"F0.imprint","INTERSECT",VERTEX,{"derivedFrom":[subQ1,subQ3]});Q101=makeQuery(id+"F0.imprint","IMPRINT",FACE,{"disambiguationData":[TD([[makeQuery(id+"F0.imprint","IMPRINT",EDGE,{"disambiguationData":[TD([[subQ4,1.0]])],"derivedFrom":subQ1}),-1.0]])]});}
            var Q102;
            {var subQ0=sQuery(id+"F0.wireOp",EDGE,"E31");var subQ1=sQuery(id+"F0.wireOp",EDGE,"E1");var subQ2=makeQuery(id+"F0.imprint","INTERSECT",VERTEX,{"derivedFrom":[subQ1,subQ0]});Q102=makeQuery(id+"F0.imprint","IMPRINT",FACE,{"disambiguationData":[TD([[makeQuery(id+"F0.imprint","IMPRINT",EDGE,{"disambiguationData":[TD([[subQ2,1.0]])],"derivedFrom":subQ1}),-1.0]])]});}
            var Q103;
            {var subQ0=sQuery(id+"F0.wireOp",EDGE,"E32");var subQ1=sQuery(id+"F0.wireOp",EDGE,"E1");var subQ2=makeQuery(id+"F0.imprint","INTERSECT",VERTEX,{"derivedFrom":[subQ1,subQ0]});Q103=makeQuery(id+"F0.imprint","IMPRINT",FACE,{"disambiguationData":[TD([[makeQuery(id+"F0.imprint","IMPRINT",EDGE,{"disambiguationData":[TD([[subQ2,-1.0]])],"derivedFrom":subQ1}),-1.0]])]});}
            var Q104;
            {var subQ1=sQuery(id+"F0.wireOp",EDGE,"E1");var subQ3=sQuery(id+"F0.wireOp",EDGE,"E30");var subQ4=makeQuery(id+"F0.imprint","INTERSECT",VERTEX,{"derivedFrom":[subQ1,subQ3]});Q104=makeQuery(id+"F0.imprint","IMPRINT",FACE,{"disambiguationData":[TD([[makeQuery(id+"F0.imprint","IMPRINT",EDGE,{"disambiguationData":[TD([[subQ4,-1.0]])],"derivedFrom":subQ1}),-1.0]])]});}
            var Q105;
            {var subQ0=sQuery(id+"F0.wireOp",EDGE,"E13");var subQ1=sQuery(id+"F0.wireOp",EDGE,"E2");var subQ2=makeQuery(id+"F0.imprint","INTERSECT",VERTEX,{"derivedFrom":[subQ1,subQ0]});Q105=makeQuery(id+"F0.imprint","IMPRINT",FACE,{"disambiguationData":[TD([[makeQuery(id+"F0.imprint","IMPRINT",EDGE,{"disambiguationData":[TD([[subQ2,1.0]])],"derivedFrom":subQ0}),-1.0]])]});}
            var Q106;
            {var subQ0=sQuery(id+"F0.wireOp",EDGE,"E11");var subQ1=sQuery(id+"F0.wireOp",EDGE,"E2");var subQ2=makeQuery(id+"F0.imprint","INTERSECT",VERTEX,{"derivedFrom":[subQ1,subQ0]});Q106=makeQuery(id+"F0.imprint","IMPRINT",FACE,{"disambiguationData":[TD([[makeQuery(id+"F0.imprint","IMPRINT",EDGE,{"disambiguationData":[TD([[subQ2,1.0]])],"derivedFrom":subQ0}),1.0]])]});}
            var Q107;
            {var subQ0=sQuery(id+"F0.wireOp",EDGE,"E13");var subQ1=sQuery(id+"F0.wireOp",EDGE,"E2");var subQ2=makeQuery(id+"F0.imprint","INTERSECT",VERTEX,{"derivedFrom":[subQ1,subQ0]});Q107=makeQuery(id+"F0.imprint","IMPRINT",FACE,{"disambiguationData":[TD([[makeQuery(id+"F0.imprint","IMPRINT",EDGE,{"disambiguationData":[TD([[subQ2,1.0]])],"derivedFrom":subQ0}),1.0]])]});}
            extrude(context, id + "F1", {"entities" : qUnion([Q0, Q1, Q2, Q3, Q4, Q5, Q6, Q7, Q8, Q9, Q10, Q11, Q12, Q13, Q14, Q15, Q16, Q17, Q18, Q19, Q20, Q21, Q22, Q23, Q24, Q25, Q26, Q27, Q28, Q29, Q30, Q31, Q32, Q33, Q34, Q35, Q36, Q37, Q38, Q39, Q40, Q41, Q42, Q43, Q44, Q45, Q46, Q47, Q48, Q49, Q50, Q51, Q52, Q53, Q54, Q55, Q56, Q57, Q58, Q59, Q60, Q61, Q62, Q63, Q64, Q65, Q66, Q67, Q68, Q69, Q70, Q71, Q72, Q73, Q74, Q75, Q76, Q77, Q78, Q79, Q80, Q81, Q82, Q83, Q84, Q85, Q86, Q87, Q88, Q89, Q90, Q91, Q92, Q93, Q94, Q95, Q96, Q97, Q98, Q99, Q100, Q101, Q102, Q103, Q104, Q105, Q106, Q107]), "depth" : 12.7 * mm, "offsetDistance" : 25.4 * mm});
        }
        {
            var Q0;
            Q0=makeQuery(id+"F1.opExtrude","SWEPT_BODY",BODY,{"disambiguationData":[OSD([sQuery(id+"F0.wireOp",EDGE,"E0"),sQuery(id+"F0.wireOp",EDGE,"E2"),sQuery(id+"F0.wireOp",EDGE,"E25"),sQuery(id+"F0.wireOp",EDGE,"E26"),sQuery(id+"F0.wireOp",EDGE,"E27"),sQuery(id+"F0.wireOp",EDGE,"E28"),sQuery(id+"F0.wireOp",EDGE,"E29"),sQuery(id+"F0.wireOp",EDGE,"E30"),sQuery(id+"F0.wireOp",EDGE,"E31"),sQuery(id+"F0.wireOp",EDGE,"E32"),sQuery(id+"F0.wireOp",EDGE,"E33"),sQuery(id+"F0.wireOp",EDGE,"E34"),sQuery(id+"F0.wireOp",EDGE,"E35"),sQuery(id+"F0.wireOp",EDGE,"E36"),sQuery(id+"F0.wireOp",EDGE,"E37"),sQuery(id+"F0.wireOp",EDGE,"E38"),sQuery(id+"F0.wireOp",EDGE,"E39"),sQuery(id+"F0.wireOp",EDGE,"E40"),sQuery(id+"F0.wireOp",EDGE,"E41"),sQuery(id+"F0.wireOp",EDGE,"E42")])]});
            var Q1;
            Q1=qCreatedBy(makeId("Origin.pointOp"),VERTEX);
            transform(context, id + "F2", {"entities" : qUnion([Q0]), "transformType" : TransformType.SCALE_UNIFORMLY, "scale" : 0.19, "scalePoint" : qUnion([Q1]), "makeCopy" : false});
        }
        {
            var Q0;
            Q0=makeQuery(id+"F1.opExtrude","CAP_FACE",FACE,{"disambiguationData":[OSD([sQuery(id+"F0.wireOp",EDGE,"E0"),sQuery(id+"F0.wireOp",EDGE,"E2"),sQuery(id+"F0.wireOp",EDGE,"E25"),sQuery(id+"F0.wireOp",EDGE,"E26"),sQuery(id+"F0.wireOp",EDGE,"E27"),sQuery(id+"F0.wireOp",EDGE,"E28"),sQuery(id+"F0.wireOp",EDGE,"E29"),sQuery(id+"F0.wireOp",EDGE,"E30"),sQuery(id+"F0.wireOp",EDGE,"E31"),sQuery(id+"F0.wireOp",EDGE,"E32"),sQuery(id+"F0.wireOp",EDGE,"E33"),sQuery(id+"F0.wireOp",EDGE,"E34"),sQuery(id+"F0.wireOp",EDGE,"E35"),sQuery(id+"F0.wireOp",EDGE,"E36"),sQuery(id+"F0.wireOp",EDGE,"E37"),sQuery(id+"F0.wireOp",EDGE,"E38"),sQuery(id+"F0.wireOp",EDGE,"E39"),sQuery(id+"F0.wireOp",EDGE,"E40"),sQuery(id+"F0.wireOp",EDGE,"E41"),sQuery(id+"F0.wireOp",EDGE,"E42")])],"isStart":false});
            extrude(context, id + "F3", {"entities" : qUnion([Q0]), "operationType" : NewBodyOperationType.ADD, "depth" : 0.8 * mm, "offsetDistance" : 25.4 * mm});
        }
        {
            var Q0;
            Q0=makeQuery(id+"F3.opExtrude","CAP_FACE",FACE,{"disambiguationData":[OSD([sQuery(id+"F0.wireOp",EDGE,"E0"),sQuery(id+"F0.wireOp",EDGE,"E2"),sQuery(id+"F0.wireOp",EDGE,"E25"),sQuery(id+"F0.wireOp",EDGE,"E26"),sQuery(id+"F0.wireOp",EDGE,"E27"),sQuery(id+"F0.wireOp",EDGE,"E28"),sQuery(id+"F0.wireOp",EDGE,"E29"),sQuery(id+"F0.wireOp",EDGE,"E30"),sQuery(id+"F0.wireOp",EDGE,"E31"),sQuery(id+"F0.wireOp",EDGE,"E32"),sQuery(id+"F0.wireOp",EDGE,"E33"),sQuery(id+"F0.wireOp",EDGE,"E34"),sQuery(id+"F0.wireOp",EDGE,"E35"),sQuery(id+"F0.wireOp",EDGE,"E36"),sQuery(id+"F0.wireOp",EDGE,"E37"),sQuery(id+"F0.wireOp",EDGE,"E38"),sQuery(id+"F0.wireOp",EDGE,"E39"),sQuery(id+"F0.wireOp",EDGE,"E40"),sQuery(id+"F0.wireOp",EDGE,"E41"),sQuery(id+"F0.wireOp",EDGE,"E42")])],"isStart":false});
            var sketch = newSketch(context, id + "F4", { "sketchPlane" : qUnion([Q0])});
            skCircle(sketch, "E43", {"center": v(0, 0) * mm, "radius": 0.8 * mm});
            skCircle(sketch, "E44", {"center": v(0, 0) * mm, "radius": 1.59 * mm});
            skSolve(sketch);
        }
        {
            var Q0;
            Q0=makeQuery(id+"F4.imprint","IMPRINT",FACE,{"disambiguationData":[TD([[makeQuery(id+"F4.imprint","IMPRINT",EDGE,{"derivedFrom":sQuery(id+"F4.wireOp",EDGE,"E43")}),-1.0]])]});
            extrude(context, id + "F5", {"entities" : qUnion([Q0]), "operationType" : NewBodyOperationType.ADD, "depth" : 6.35 * mm, "offsetDistance" : 25.4 * mm});
        }
        {
            var Q0;
            Q0=makeQuery(id+"F5.boolean.opBoolean","SPLIT",FACE,{"disambiguationData":[TD([makeQuery(id+"F5.opExtrude","SWEPT_FACE",FACE,{"disambiguationData":[OSD([sQuery(id+"F4.wireOp",EDGE,"E43")])]})])],"derivedFrom":makeQuery(id+"F3.opExtrude","CAP_FACE",FACE,{"disambiguationData":[OSD([sQuery(id+"F0.wireOp",EDGE,"E0"),sQuery(id+"F0.wireOp",EDGE,"E2"),sQuery(id+"F0.wireOp",EDGE,"E25"),sQuery(id+"F0.wireOp",EDGE,"E26"),sQuery(id+"F0.wireOp",EDGE,"E27"),sQuery(id+"F0.wireOp",EDGE,"E28"),sQuery(id+"F0.wireOp",EDGE,"E29"),sQuery(id+"F0.wireOp",EDGE,"E30"),sQuery(id+"F0.wireOp",EDGE,"E31"),sQuery(id+"F0.wireOp",EDGE,"E32"),sQuery(id+"F0.wireOp",EDGE,"E33"),sQuery(id+"F0.wireOp",EDGE,"E34"),sQuery(id+"F0.wireOp",EDGE,"E35"),sQuery(id+"F0.wireOp",EDGE,"E36"),sQuery(id+"F0.wireOp",EDGE,"E37"),sQuery(id+"F0.wireOp",EDGE,"E38"),sQuery(id+"F0.wireOp",EDGE,"E39"),sQuery(id+"F0.wireOp",EDGE,"E40"),sQuery(id+"F0.wireOp",EDGE,"E41"),sQuery(id+"F0.wireOp",EDGE,"E42")])],"isStart":false})});
            extrude(context, id + "F6", {"entities" : qUnion([Q0]), "operationType" : NewBodyOperationType.REMOVE, "oppositeDirection" : true, "depth" : 25.4 * mm, "offsetDistance" : 25.4 * mm});
        }
    });
